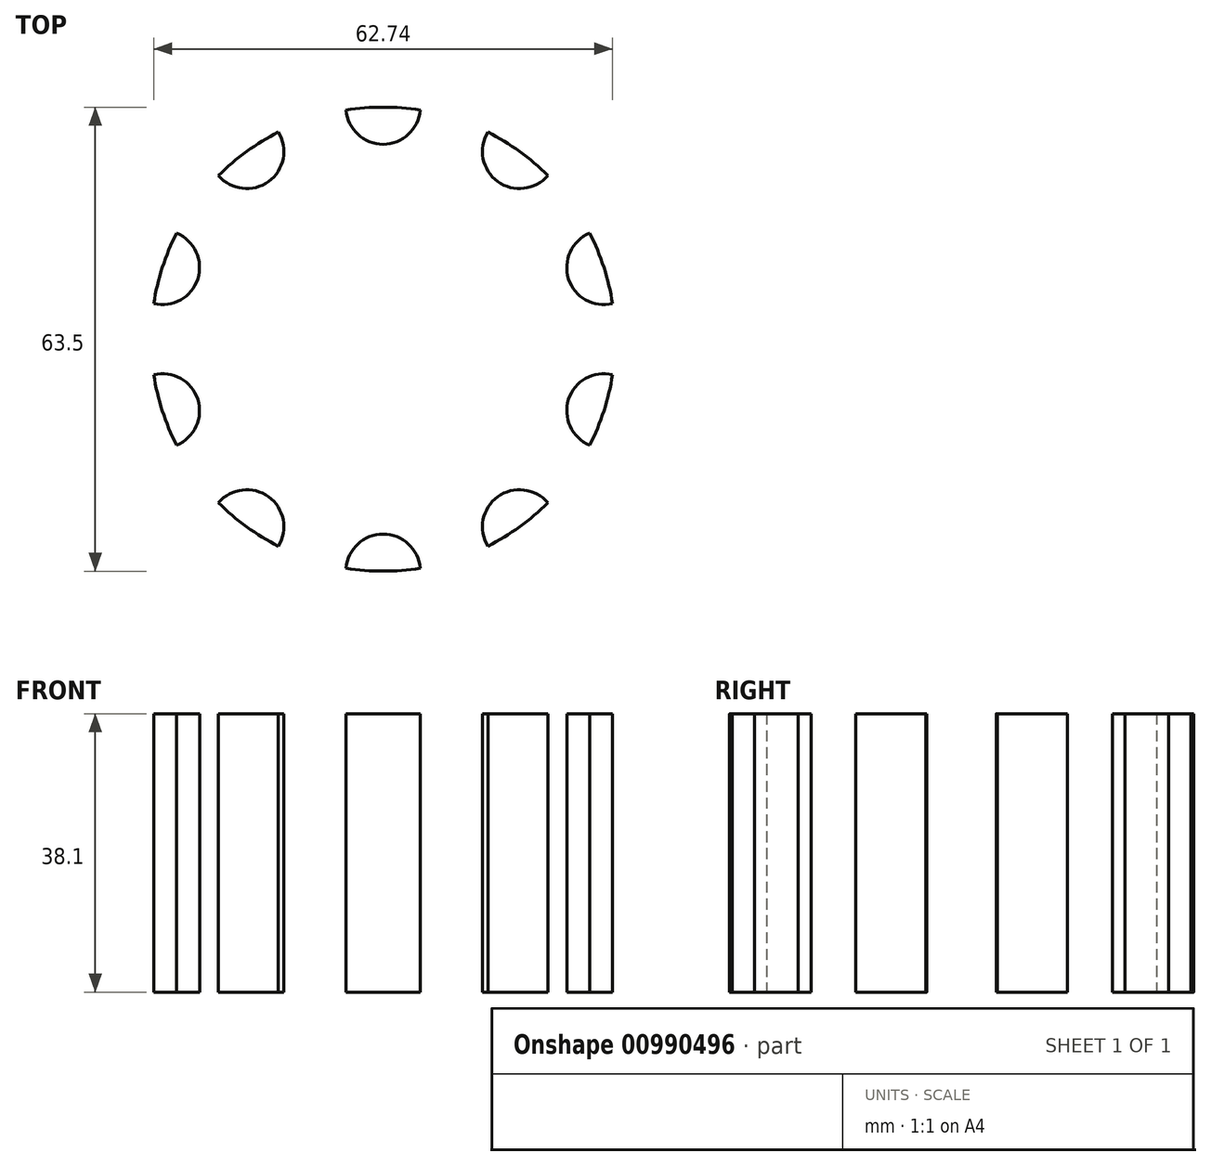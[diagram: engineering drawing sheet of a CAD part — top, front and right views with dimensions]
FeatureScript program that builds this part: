
annotation { "Feature Type Name" : "Feature", "Feature Type Description" : "" }
export const myFeature = defineFeature(function(context is Context, id is Id, definition is map)
    precondition{}
    {
        {
            var Q0;
            Q0=qCreatedBy(makeId("Top.planeOp"),FACE);
            var sketch = newSketch(context, id + "F0", { "sketchPlane" : qUnion([Q0])});
            skCircle(sketch, "E0", {"center": v(0, 0) * mm, "radius": 31.75 * mm});
            skSolve(sketch);
        }
        {
            var Q0;
            Q0=makeQuery(id+"F0.imprint","IMPRINT",FACE,{"disambiguationData":[TD([[makeQuery(id+"F0.imprint","IMPRINT",EDGE,{"derivedFrom":sQuery(id+"F0.wireOp",EDGE,"E0")}),1.0]])]});
            extrude(context, id + "F1", {"entities" : qUnion([Q0]), "depth" : 38.1 * mm});
        }
        {
            var Q0;
            Q0=qCreatedBy(makeId("Top.planeOp"),FACE);
            var sketch = newSketch(context, id + "F2", { "sketchPlane" : qUnion([Q0])});
            skCircle(sketch, "E1", {"center": v(0, 31.75) * mm, "radius": 5.08 * mm});
            skCircle(sketch, "E2.1.0", {"center": v(-18.66, 25.69) * mm, "radius": 5.08 * mm});
            skCircle(sketch, "E2.2.0", {"center": v(-30.2, 9.81) * mm, "radius": 5.08 * mm});
            skCircle(sketch, "E2.3.0", {"center": v(-30.2, -9.81) * mm, "radius": 5.08 * mm});
            skCircle(sketch, "E2.4.0", {"center": v(-18.66, -25.69) * mm, "radius": 5.08 * mm});
            skCircle(sketch, "E2.5.0", {"center": v(0, -31.75) * mm, "radius": 5.08 * mm});
            skCircle(sketch, "E2.6.0", {"center": v(18.66, -25.69) * mm, "radius": 5.08 * mm});
            skCircle(sketch, "E2.7.0", {"center": v(30.2, -9.81) * mm, "radius": 5.08 * mm});
            skCircle(sketch, "E2.8.0", {"center": v(30.2, 9.81) * mm, "radius": 5.08 * mm});
            skCircle(sketch, "E2.9.0", {"center": v(18.66, 25.69) * mm, "radius": 5.08 * mm});
            skPoint(sketch, "E2.center", {"position": v(0, 0) * mm});
            skSolve(sketch);
        }
        {
            var Q0;
            Q0=qSketchRegion(id+"F2",true);
            extrude(context, id + "F3", {"entities" : qUnion([Q0]), "depth" : 50.8 * mm});
        }
        {
            var Q0;
            Q0=makeQuery(id+"F1.opExtrude","SWEPT_BODY",BODY,{"disambiguationData":[OSD([sQuery(id+"F0.wireOp",EDGE,"E0")])]});
            var Q1;
            Q1=makeQuery(id+"F3.opExtrude","SWEPT_BODY",BODY,{"disambiguationData":[OSD([sQuery(id+"F2.wireOp",EDGE,"E2.5.0")])]});
            booleanBodies(context, id + "F4", {"operationType" : BooleanOperationType.INTERSECTION, "tools" : qUnion([Q0, Q1]), "keepTools" : true});
        }
        {
            var Q0;
            Q0=makeQuery(id+"F1.opExtrude","SWEPT_BODY",BODY,{"disambiguationData":[OSD([sQuery(id+"F0.wireOp",EDGE,"E0")])]});
            var Q1;
            Q1=makeQuery(id+"F3.opExtrude","SWEPT_BODY",BODY,{"disambiguationData":[OSD([sQuery(id+"F2.wireOp",EDGE,"E2.6.0")])]});
            booleanBodies(context, id + "F5", {"operationType" : BooleanOperationType.INTERSECTION, "tools" : qUnion([Q0, Q1]), "keepTools" : true});
        }
        {
            var Q0;
            Q0=makeQuery(id+"F3.opExtrude","SWEPT_BODY",BODY,{"disambiguationData":[OSD([sQuery(id+"F2.wireOp",EDGE,"E2.7.0")])]});
            var Q1;
            Q1=makeQuery(id+"F1.opExtrude","SWEPT_BODY",BODY,{"disambiguationData":[OSD([sQuery(id+"F0.wireOp",EDGE,"E0")])]});
            booleanBodies(context, id + "F6", {"operationType" : BooleanOperationType.INTERSECTION, "tools" : qUnion([Q0, Q1]), "keepTools" : true});
        }
        {
            var Q0;
            Q0=makeQuery(id+"F3.opExtrude","SWEPT_BODY",BODY,{"disambiguationData":[OSD([sQuery(id+"F2.wireOp",EDGE,"E2.8.0")])]});
            var Q1;
            Q1=makeQuery(id+"F1.opExtrude","SWEPT_BODY",BODY,{"disambiguationData":[OSD([sQuery(id+"F0.wireOp",EDGE,"E0")])]});
            booleanBodies(context, id + "F7", {"operationType" : BooleanOperationType.INTERSECTION, "tools" : qUnion([Q0, Q1]), "keepTools" : true});
        }
        {
            var Q0;
            Q0=makeQuery(id+"F1.opExtrude","SWEPT_BODY",BODY,{"disambiguationData":[OSD([sQuery(id+"F0.wireOp",EDGE,"E0")])]});
            var Q1;
            Q1=makeQuery(id+"F3.opExtrude","SWEPT_BODY",BODY,{"disambiguationData":[OSD([sQuery(id+"F2.wireOp",EDGE,"E2.9.0")])]});
            booleanBodies(context, id + "F8", {"operationType" : BooleanOperationType.INTERSECTION, "tools" : qUnion([Q0, Q1]), "keepTools" : true});
        }
        {
            var Q0;
            Q0=makeQuery(id+"F3.opExtrude","SWEPT_BODY",BODY,{"disambiguationData":[OSD([sQuery(id+"F2.wireOp",EDGE,"E1")])]});
            var Q1;
            Q1=makeQuery(id+"F1.opExtrude","SWEPT_BODY",BODY,{"disambiguationData":[OSD([sQuery(id+"F0.wireOp",EDGE,"E0")])]});
            booleanBodies(context, id + "F9", {"operationType" : BooleanOperationType.INTERSECTION, "tools" : qUnion([Q0, Q1]), "keepTools" : true});
        }
        {
            var Q0;
            Q0=makeQuery(id+"F3.opExtrude","SWEPT_BODY",BODY,{"disambiguationData":[OSD([sQuery(id+"F2.wireOp",EDGE,"E2.1.0")])]});
            var Q1;
            Q1=makeQuery(id+"F1.opExtrude","SWEPT_BODY",BODY,{"disambiguationData":[OSD([sQuery(id+"F0.wireOp",EDGE,"E0")])]});
            booleanBodies(context, id + "F10", {"operationType" : BooleanOperationType.INTERSECTION, "tools" : qUnion([Q0, Q1]), "keepTools" : true});
        }
        {
            var Q0;
            Q0=makeQuery(id+"F3.opExtrude","SWEPT_BODY",BODY,{"disambiguationData":[OSD([sQuery(id+"F2.wireOp",EDGE,"E2.2.0")])]});
            var Q1;
            Q1=makeQuery(id+"F1.opExtrude","SWEPT_BODY",BODY,{"disambiguationData":[OSD([sQuery(id+"F0.wireOp",EDGE,"E0")])]});
            booleanBodies(context, id + "F11", {"operationType" : BooleanOperationType.INTERSECTION, "tools" : qUnion([Q0, Q1]), "keepTools" : true});
        }
        {
            var Q0;
            Q0=makeQuery(id+"F3.opExtrude","SWEPT_BODY",BODY,{"disambiguationData":[OSD([sQuery(id+"F2.wireOp",EDGE,"E2.3.0")])]});
            var Q1;
            Q1=makeQuery(id+"F1.opExtrude","SWEPT_BODY",BODY,{"disambiguationData":[OSD([sQuery(id+"F0.wireOp",EDGE,"E0")])]});
            booleanBodies(context, id + "F12", {"operationType" : BooleanOperationType.INTERSECTION, "tools" : qUnion([Q0, Q1]), "keepTools" : true});
        }
        {
            var Q0;
            Q0=makeQuery(id+"F3.opExtrude","SWEPT_BODY",BODY,{"disambiguationData":[OSD([sQuery(id+"F2.wireOp",EDGE,"E2.4.0")])]});
            var Q1;
            Q1=makeQuery(id+"F1.opExtrude","SWEPT_BODY",BODY,{"disambiguationData":[OSD([sQuery(id+"F0.wireOp",EDGE,"E0")])]});
            booleanBodies(context, id + "F13", {"operationType" : BooleanOperationType.INTERSECTION, "tools" : qUnion([Q0, Q1]), "keepTools" : true});
        }
        {
            var Q0;
            Q0=makeQuery(id+"F3.opExtrude","SWEPT_BODY",BODY,{"disambiguationData":[OSD([sQuery(id+"F2.wireOp",EDGE,"E2.3.0")])]});
            var Q1;
            Q1=makeQuery(id+"F3.opExtrude","SWEPT_BODY",BODY,{"disambiguationData":[OSD([sQuery(id+"F2.wireOp",EDGE,"E2.4.0")])]});
            var Q2;
            Q2=makeQuery(id+"F3.opExtrude","SWEPT_BODY",BODY,{"disambiguationData":[OSD([sQuery(id+"F2.wireOp",EDGE,"E2.5.0")])]});
            var Q3;
            Q3=makeQuery(id+"F3.opExtrude","SWEPT_BODY",BODY,{"disambiguationData":[OSD([sQuery(id+"F2.wireOp",EDGE,"E2.6.0")])]});
            var Q4;
            Q4=makeQuery(id+"F3.opExtrude","SWEPT_BODY",BODY,{"disambiguationData":[OSD([sQuery(id+"F2.wireOp",EDGE,"E2.7.0")])]});
            var Q5;
            Q5=makeQuery(id+"F3.opExtrude","SWEPT_BODY",BODY,{"disambiguationData":[OSD([sQuery(id+"F2.wireOp",EDGE,"E2.8.0")])]});
            var Q6;
            Q6=makeQuery(id+"F3.opExtrude","SWEPT_BODY",BODY,{"disambiguationData":[OSD([sQuery(id+"F2.wireOp",EDGE,"E2.9.0")])]});
            var Q7;
            Q7=makeQuery(id+"F3.opExtrude","SWEPT_BODY",BODY,{"disambiguationData":[OSD([sQuery(id+"F2.wireOp",EDGE,"E1")])]});
            var Q8;
            Q8=makeQuery(id+"F3.opExtrude","SWEPT_BODY",BODY,{"disambiguationData":[OSD([sQuery(id+"F2.wireOp",EDGE,"E2.1.0")])]});
            var Q9;
            Q9=makeQuery(id+"F3.opExtrude","SWEPT_BODY",BODY,{"disambiguationData":[OSD([sQuery(id+"F2.wireOp",EDGE,"E2.2.0")])]});
            var Q10;
            Q10=makeQuery(id+"F1.opExtrude","SWEPT_BODY",BODY,{"disambiguationData":[OSD([sQuery(id+"F0.wireOp",EDGE,"E0")])]});
            booleanBodies(context, id + "F14", {"operationType" : BooleanOperationType.INTERSECTION, "tools" : qUnion([Q0, Q1, Q2, Q3, Q4, Q5, Q6, Q7, Q8, Q9, Q10])});
        }
    });
